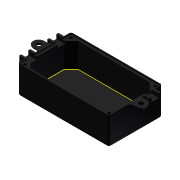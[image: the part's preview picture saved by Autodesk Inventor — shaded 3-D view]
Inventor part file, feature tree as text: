
AUTODESK INVENTOR PART (.ipt)
format: ipt  version: 2012 (Build 160160000, 160)  size: 399,360 bytes
history: native  units: mm
features: sketch x13, extrude x8, fillet x4, hole x2, other x1
ambient origin geometry x8: Origin, YZ Plane, XZ Plane, XY Plane, X Axis, Y Axis, Z Axis, Center Point
feature tree (28):
  other  "Твердое тело1"
  extrude  "Выдавливание1"  Depth=65.0mm
  extrude  "Выдавливание5"  Depth=65.0mm
  sketch  "Эскиз10"
  extrude  "Выдавливание8"  Depth=1.5mm TaperAngle=0.0deg
  extrude  "Выдавливание9"  Depth=2.0mm
  extrude  "Выдавливание10"  Depth=2.0mm
  sketch  "Эскиз15"
  sketch  "Эскиз16"
  sketch  "Эскиз17"
  extrude  "Выдавливание11"  Depth=2.0mm
  extrude  "Выдавливание12"  Depth=2.0mm
  sketch  "Эскиз18"
  extrude  "Выдавливание13"  Depth=5.0mm
  hole  "Отверстие1"  [1 undecoded]
  hole  "Отверстие2"  [1 undecoded]
  fillet  "Сопряжение4"  [1 undecoded]
  fillet  "Сопряжение5"  Radius=5.0mm
  fillet  "Сопряжение6"  [1 undecoded]
  fillet  "Сопряжение7"  Radius=5.0mm
  sketch  "Эскиз1"
  sketch  "Эскиз7"
  sketch  "Эскиз12"
  sketch  "Эскиз13"
  sketch  "Эскиз14"
  sketch  "Эскиз19"
  sketch  "Эскиз20"
  sketch  "Эскиз21"
note: 4 required parameter values undecoded (feature->parameter linkage not recoverable at this tier; creation-order binding heuristic only, values carry confidence <= 0.55)
